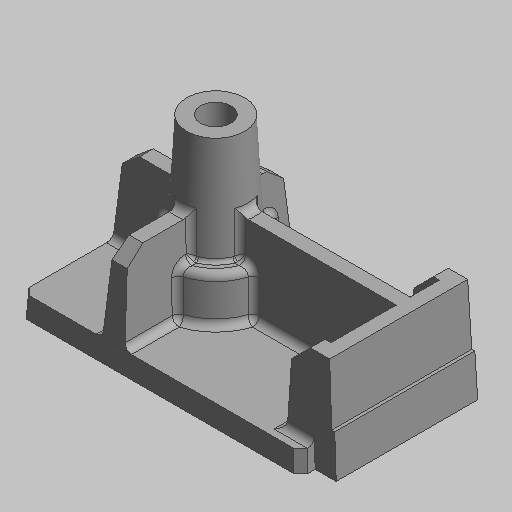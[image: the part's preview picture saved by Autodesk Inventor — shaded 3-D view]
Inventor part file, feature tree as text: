
AUTODESK INVENTOR PART (.ipt)
format: ipt  version: 2023.5 (Build 275446000, 446)  size: 418,304 bytes
history: native  units: mm (DEFAULTED — no unit token found)
features: fillet x1
ambient origin geometry x8: Origin, YZ Plane, XZ Plane, XY Plane, X Axis, Y Axis, Z Axis, Center Point
bodies: Solid1 (feature_tree)
feature tree (1):
  fillet  "Fillet10"  [1 undecoded]
note: 1 required parameter value undecoded (feature->parameter linkage not recoverable at this tier; creation-order binding heuristic only, values carry confidence <= 0.55)
